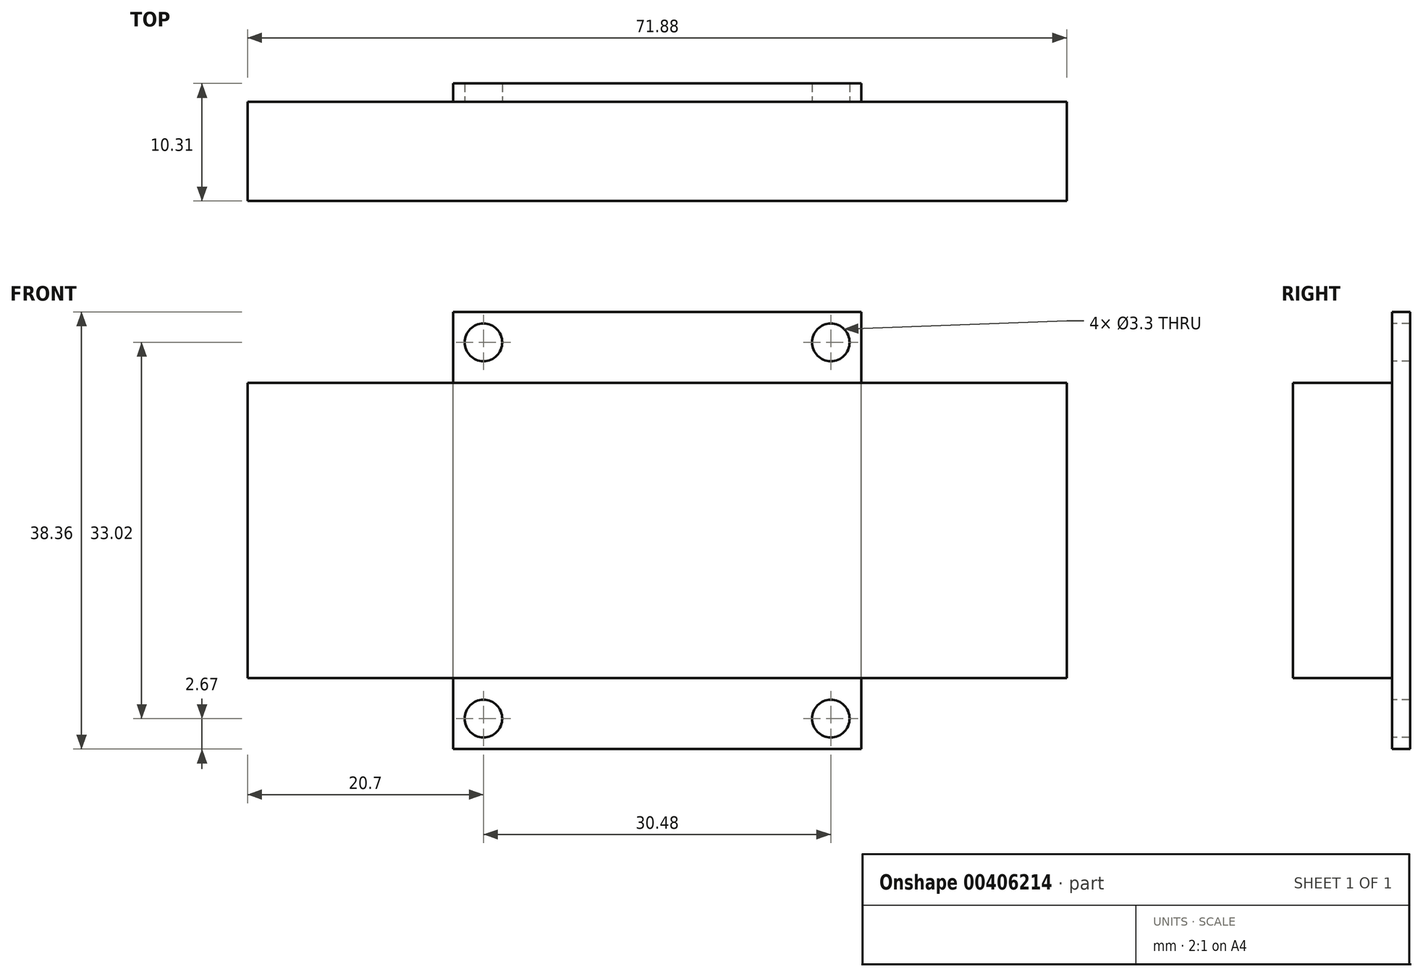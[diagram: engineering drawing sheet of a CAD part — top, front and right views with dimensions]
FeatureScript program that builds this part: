
annotation { "Feature Type Name" : "Feature", "Feature Type Description" : "" }
export const myFeature = defineFeature(function(context is Context, id is Id, definition is map)
    precondition{}
    {
        {
            var Q0;
            Q0=qCreatedBy(makeId("Front.planeOp"),FACE);
            var sketch = newSketch(context, id + "F0", { "sketchPlane" : qUnion([Q0])});
            skLineSegment(sketch, "E0.bottom", {"start": v(35.94, -12.95) * mm, "end": v(-35.94, -12.95) * mm});
            skLineSegment(sketch, "E0.top", {"start": v(35.94, 12.95) * mm, "end": v(-35.94, 12.95) * mm});
            skLineSegment(sketch, "E0.left", {"start": v(35.94, -12.95) * mm, "end": v(35.94, 12.95) * mm});
            skLineSegment(sketch, "E0.right", {"start": v(-35.94, -12.95) * mm, "end": v(-35.94, 12.95) * mm});
            skPoint(sketch, "E0.middle", {"position": v(0, 0) * mm});
            skLineSegment(sketch, "E1.bottom", {"start": v(17.9, -19.18) * mm, "end": v(-17.9, -19.18) * mm});
            skLineSegment(sketch, "E1.top", {"start": v(17.9, 19.18) * mm, "end": v(-17.9, 19.18) * mm});
            skLineSegment(sketch, "E1.left", {"start": v(17.9, -19.18) * mm, "end": v(17.9, 19.18) * mm});
            skLineSegment(sketch, "E1.right", {"start": v(-17.9, -19.18) * mm, "end": v(-17.9, 19.18) * mm});
            skCircle(sketch, "E2", {"center": v(-15.24, 16.5) * mm, "radius": 1.65 * mm});
            skCircle(sketch, "E3", {"center": v(15.24, 16.51) * mm, "radius": 1.65 * mm});
            skCircle(sketch, "E4", {"center": v(15.24, -16.51) * mm, "radius": 1.65 * mm});
            skCircle(sketch, "E5", {"center": v(-15.24, -16.51) * mm, "radius": 1.65 * mm});
            skSolve(sketch);
        }
        {
            var Q0;
            {var subQ0=sQuery(id+"F0.wireOp",EDGE,"E0.right");Q0=makeQuery(id+"F0.imprint","IMPRINT",FACE,{"disambiguationData":[TD([[makeQuery(id+"F0.imprint","IMPRINT",EDGE,{"derivedFrom":subQ0}),-1.0]])]});}
            var Q1;
            {var subQ0=sQuery(id+"F0.wireOp",EDGE,"E1.left");var subQ1=sQuery(id+"F0.wireOp",EDGE,"E0.bottom");var subQ2=makeQuery(id+"F0.imprint","INTERSECT",VERTEX,{"derivedFrom":[subQ1,subQ0]});Q1=makeQuery(id+"F0.imprint","IMPRINT",FACE,{"disambiguationData":[TD([[makeQuery(id+"F0.imprint","IMPRINT",EDGE,{"disambiguationData":[TD([[subQ2,-1.0]])],"derivedFrom":subQ1}),-1.0]])]});}
            var Q2;
            {var subQ0=sQuery(id+"F0.wireOp",EDGE,"E0.left");Q2=makeQuery(id+"F0.imprint","IMPRINT",FACE,{"disambiguationData":[TD([[makeQuery(id+"F0.imprint","IMPRINT",EDGE,{"derivedFrom":subQ0}),1.0]])]});}
            extrude(context, id + "F1", {"entities" : qUnion([Q0, Q1, Q2]), "depth" : 8.71 * mm});
        }
        {
            var Q0;
            {var subQ0=sQuery(id+"F0.wireOp",EDGE,"E1.left");var subQ1=sQuery(id+"F0.wireOp",EDGE,"E0.bottom");var subQ2=makeQuery(id+"F0.imprint","INTERSECT",VERTEX,{"derivedFrom":[subQ1,subQ0]});Q0=makeQuery(id+"F0.imprint","IMPRINT",FACE,{"disambiguationData":[TD([[makeQuery(id+"F0.imprint","IMPRINT",EDGE,{"disambiguationData":[TD([[subQ2,-1.0]])],"derivedFrom":subQ1}),-1.0]])]});}
            var Q1;
            {var subQ1=sQuery(id+"F0.wireOp",EDGE,"E1.bottom");Q1=makeQuery(id+"F0.imprint","IMPRINT",FACE,{"disambiguationData":[TD([[makeQuery(id+"F0.imprint","IMPRINT",EDGE,{"derivedFrom":subQ1}),-1.0]])]});}
            var Q2;
            {var subQ1=sQuery(id+"F0.wireOp",EDGE,"E1.top");Q2=makeQuery(id+"F0.imprint","IMPRINT",FACE,{"disambiguationData":[TD([[makeQuery(id+"F0.imprint","IMPRINT",EDGE,{"derivedFrom":subQ1}),1.0]])]});}
            extrude(context, id + "F2", {"entities" : qUnion([Q0, Q1, Q2]), "operationType" : NewBodyOperationType.ADD, "oppositeDirection" : true, "depth" : 1.6 * mm});
        }
    });
